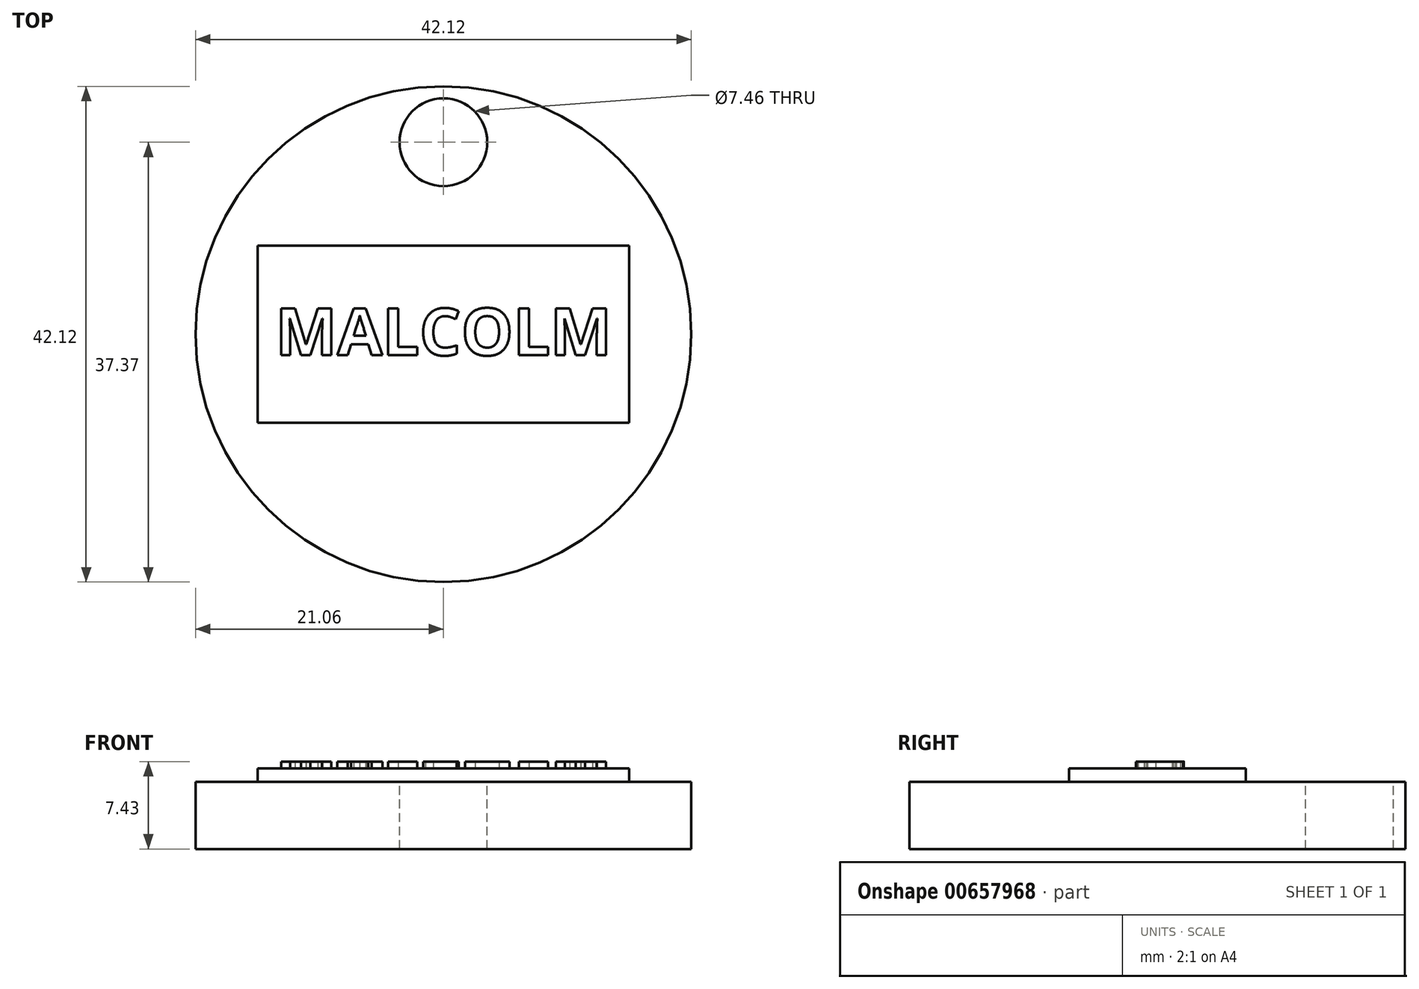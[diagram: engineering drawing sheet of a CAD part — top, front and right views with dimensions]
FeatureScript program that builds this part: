
annotation { "Feature Type Name" : "Feature", "Feature Type Description" : "" }
export const myFeature = defineFeature(function(context is Context, id is Id, definition is map)
    precondition{}
    {
        {
            var Q0;
            Q0=qCreatedBy(makeId("Top.planeOp"),FACE);
            var sketch = newSketch(context, id + "F0", { "sketchPlane" : qUnion([Q0])});
            skCircle(sketch, "E0", {"center": v(0, 6.42) * mm, "radius": 46.27 * mm});
            skSolve(sketch);
        }
        {
            var Q0;
            Q0=makeQuery(id+"F0.imprint","IMPRINT",FACE,{"disambiguationData":[TD([[makeQuery(id+"F0.imprint","IMPRINT",EDGE,{"derivedFrom":sQuery(id+"F0.wireOp",EDGE,"E0")}),1.0]])]});
            extrude(context, id + "F1", {"entities" : qUnion([Q0]), "depth" : 25.4 * mm, "offsetDistance" : 25.4 * mm});
        }
        {
            var Q0;
            Q0=makeQuery(id+"F1.opExtrude","CAP_FACE",FACE,{"disambiguationData":[OSD([sQuery(id+"F0.wireOp",EDGE,"E0")])],"isStart":false});
            var sketch = newSketch(context, id + "F2", { "sketchPlane" : qUnion([Q0])});
            skLineSegment(sketch, "E1", {"start": v(-34.46, 37.29) * mm, "end": v(35.83, -22.86) * mm});
            skCircle(sketch, "E2", {"center": v(26.75, -15.1) * mm, "radius": 10.37 * mm});
            skSolve(sketch);
        }
        {
            var Q0;
            Q0 = qSketchRegion(id + "F2", true);
            extrude(context, id + "F3", {"entities" : qUnion([Q0]), "operationType" : NewBodyOperationType.REMOVE, "oppositeDirection" : true, "depth" : 25.4 * mm, "offsetDistance" : 25.4 * mm});
        }
        {
            var Q0;
            Q0=makeQuery(id+"F1.opExtrude","SWEPT_BODY",BODY,{"disambiguationData":[OSD([sQuery(id+"F0.wireOp",EDGE,"E0")])]});
            deleteBodies(context, id + "F4", {"entities" : qUnion([Q0])});
        }
        {
            var Q0;
            Q0=qCreatedBy(makeId("Top.planeOp"),FACE);
            var sketch = newSketch(context, id + "F5", { "sketchPlane" : qUnion([Q0])});
            skCircle(sketch, "E3", {"center": v(0, 0) * mm, "radius": 46.8 * mm});
            skSolve(sketch);
        }
        {
            var Q0;
            Q0=makeQuery(id+"F5.imprint","IMPRINT",FACE,{"disambiguationData":[TD([[makeQuery(id+"F5.imprint","IMPRINT",EDGE,{"derivedFrom":sQuery(id+"F5.wireOp",EDGE,"E3")}),1.0]])]});
            extrude(context, id + "F6", {"entities" : qUnion([Q0]), "depth" : 12.7 * mm, "offsetDistance" : 25.4 * mm});
        }
        {
            var Q0;
            Q0=makeQuery(id+"F6.opExtrude","CAP_FACE",FACE,{"disambiguationData":[OSD([sQuery(id+"F5.wireOp",EDGE,"E3")])],"isStart":false});
            var sketch = newSketch(context, id + "F7", { "sketchPlane" : qUnion([Q0])});
            skLineSegment(sketch, "E4", {"start": v(0, -46.8) * mm, "end": v(0, 46.8) * mm});
            skCircle(sketch, "E5", {"center": v(0, 36.25) * mm, "radius": 8.29 * mm});
            skSolve(sketch);
        }
        {
            var Q0;
            Q0 = qSketchRegion(id + "F7", true);
            extrude(context, id + "F8", {"entities" : qUnion([Q0]), "operationType" : NewBodyOperationType.REMOVE, "oppositeDirection" : true, "depth" : 25.4 * mm, "offsetDistance" : 25.4 * mm});
        }
        {
            var Q0;
            Q0=makeQuery(id+"F6.opExtrude","CAP_FACE",FACE,{"disambiguationData":[OSD([sQuery(id+"F5.wireOp",EDGE,"E3")])],"isStart":false});
            var sketch = newSketch(context, id + "F9", { "sketchPlane" : qUnion([Q0])});
            skLineSegment(sketch, "E6.bottom", {"start": v(-35.04, -16.7) * mm, "end": v(35.04, -16.7) * mm});
            skLineSegment(sketch, "E6.top", {"start": v(-35.04, 16.7) * mm, "end": v(35.04, 16.7) * mm});
            skLineSegment(sketch, "E6.left", {"start": v(-35.04, -16.7) * mm, "end": v(-35.04, 16.7) * mm});
            skLineSegment(sketch, "E6.right", {"start": v(35.04, -16.7) * mm, "end": v(35.04, 16.7) * mm});
            skPoint(sketch, "E6.middle", {"position": v(0, 0) * mm});
            skSolve(sketch);
        }
        {
            var Q0;
            Q0=makeQuery(id+"F9.imprint","IMPRINT",FACE,{"disambiguationData":[TD([[makeQuery(id+"F9.imprint","IMPRINT",EDGE,{"derivedFrom":sQuery(id+"F9.wireOp",EDGE,"E6.bottom")}),1.0]])]});
            extrude(context, id + "F10", {"entities" : qUnion([Q0]), "operationType" : NewBodyOperationType.ADD, "depth" : 2.54 * mm, "offsetDistance" : 25.4 * mm});
        }
        {
            var Q0;
            Q0=makeQuery(id+"F10.opExtrude","CAP_FACE",FACE,{"disambiguationData":[OSD([sQuery(id+"F9.wireOp",EDGE,"E6.bottom"),sQuery(id+"F9.wireOp",EDGE,"E6.top"),sQuery(id+"F9.wireOp",EDGE,"E6.left"),sQuery(id+"F9.wireOp",EDGE,"E6.right")])],"isStart":false});
            var sketch = newSketch(context, id + "F11", { "sketchPlane" : qUnion([Q0])});
            skText(sketch, "E7", { "text": "MALCOLM", "fontName": "OpenSans-Bold.ttf"});
            const initialGuessF11  = {"E7": [-0.0317, -0.00398, 1, 0, 0.0089]};
            skSetInitialGuess(sketch, initialGuessF11);
            skSolve(sketch);
        }
        {
            var Q0;
            Q0 = qSketchRegion(id + "F11", true);
            extrude(context, id + "F12", {"entities" : qUnion([Q0]), "operationType" : NewBodyOperationType.ADD, "depth" : 1.27 * mm, "offsetDistance" : 25.4 * mm});
        }
        {
            var Q0;
            Q0=makeQuery(id+"F6.opExtrude","SWEPT_BODY",BODY,{"disambiguationData":[OSD([sQuery(id+"F5.wireOp",EDGE,"E3")])]});
            var Q1;
            Q1=qCreatedBy(makeId("Origin.pointOp"),VERTEX);
            transform(context, id + "F13", {"entities" : qUnion([Q0]), "transformType" : TransformType.SCALE_UNIFORMLY, "scale" : .45, "scalePoint" : qUnion([Q1]), "makeCopy" : false});
        }
    });
